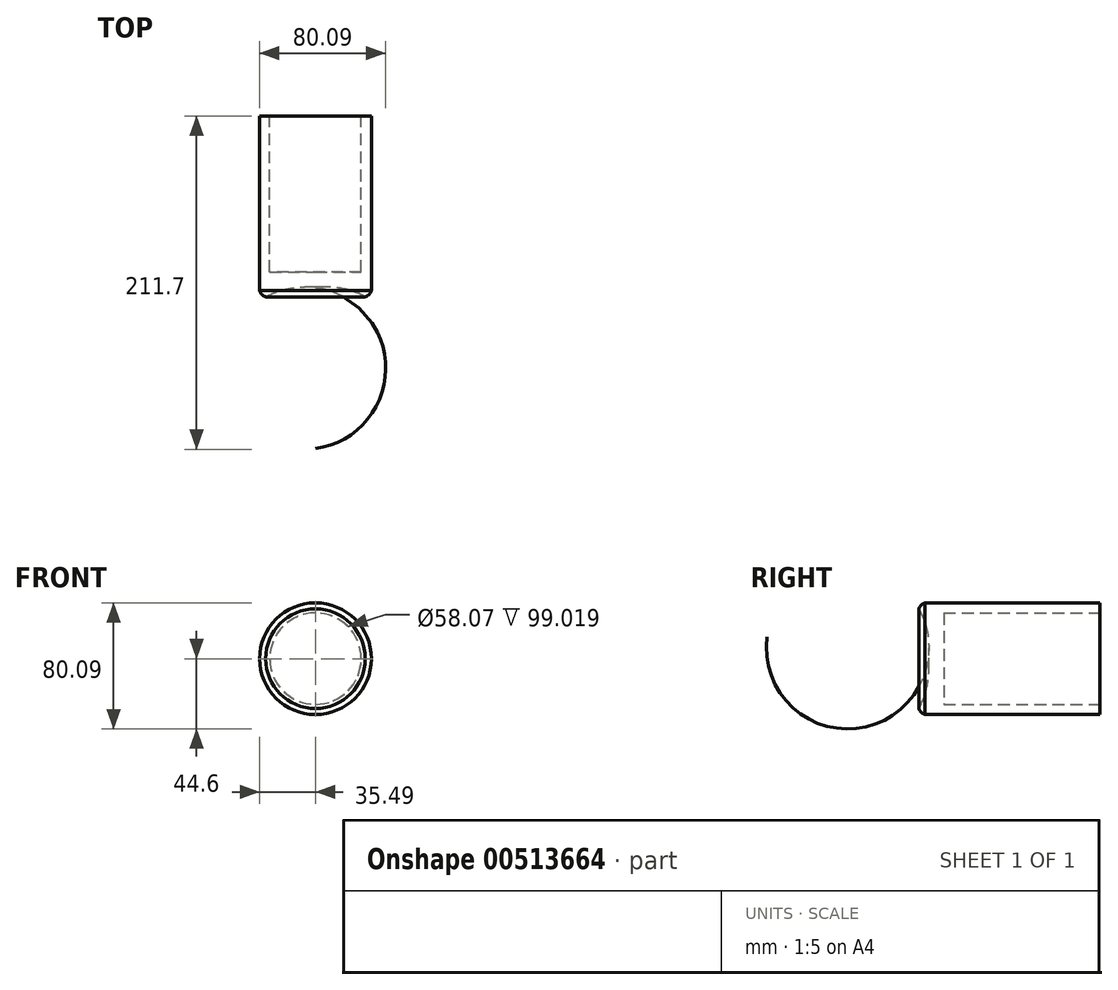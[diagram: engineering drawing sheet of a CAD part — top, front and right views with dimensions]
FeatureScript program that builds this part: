
annotation { "Feature Type Name" : "Feature", "Feature Type Description" : "" }
export const myFeature = defineFeature(function(context is Context, id is Id, definition is map)
    precondition{}
    {
        {
            var Q0;
            Q0=qCreatedBy(makeId("Top.planeOp"),FACE);
            var sketch = newSketch(context, id + "F0", { "sketchPlane" : qUnion([Q0])});
            skArc(sketch, "E0", {"start": v(31.62, -75.17) * mm, "mid": v(16.27, -69.74) * mm, "end": v(0, -69.37) * mm});
            skArc(sketch, "E1", {"start": v(31.62, -75.17) * mm, "mid": v(34.04, -73.72) * mm, "end": v(35.49, -71.3) * mm});
            skLineSegment(sketch, "E2", {"start": v(35.49, -71.3) * mm, "end": v(35.49, 39.68) * mm});
            skArc(sketch, "E3", {"start": v(0, 37.1) * mm, "mid": v(18, 34.92) * mm, "end": v(35.49, 39.68) * mm});
            skLineSegment(sketch, "E4", {"start": v(35.49, 39.68) * mm, "end": v(29.04, 39.68) * mm});
            skLineSegment(sketch, "E5", {"start": v(29.04, 39.68) * mm, "end": v(29.04, 42.26) * mm});
            skLineSegment(sketch, "E6", {"start": v(29.04, 42.26) * mm, "end": v(0, 42.26) * mm});
            skLineSegment(sketch, "E7", {"start": v(0, 42.26) * mm, "end": v(0, -69.37) * mm});
            skLineSegment(sketch, "E8", {"start": v(0, 75.81) * mm, "end": v(0, -76.79) * mm, "construction": true});
            skSolve(sketch);
        }
        {
            var Q0;
            {var subQ1=sQuery(id+"F0.wireOp",EDGE,"E3");Q0=makeQuery(id+"F0.imprint","IMPRINT",FACE,{"disambiguationData":[TD([[makeQuery(id+"F0.imprint","IMPRINT",EDGE,{"derivedFrom":subQ1}),1.0]])]});}
            var Q1;
            {var subQ1=sQuery(id+"F0.wireOp",EDGE,"E0");Q1=makeQuery(id+"F0.imprint","IMPRINT",FACE,{"disambiguationData":[TD([[makeQuery(id+"F0.imprint","IMPRINT",EDGE,{"derivedFrom":subQ1}),-1.0]])]});}
            var Q2;
            Q2=sQuery(id+"F0.wireOp",EDGE,"E8");
            revolve(context, id + "F1", {"entities" : qUnion([Q0, Q1]), "axis" : qUnion([Q2]), "revolveType" : RevolveType.FULL});
        }
        {
            var Q0;
            Q0=makeQuery(id+"F1.opRevolve","SWEPT_FACE",FACE,{"disambiguationData":[OSD([sQuery(id+"F0.wireOp",EDGE,"E6")])]});
            extrude(context, id + "F2", {"entities" : qUnion([Q0]), "operationType" : NewBodyOperationType.REMOVE, "oppositeDirection" : true, "depth" : 101.6 * mm});
        }
    });
